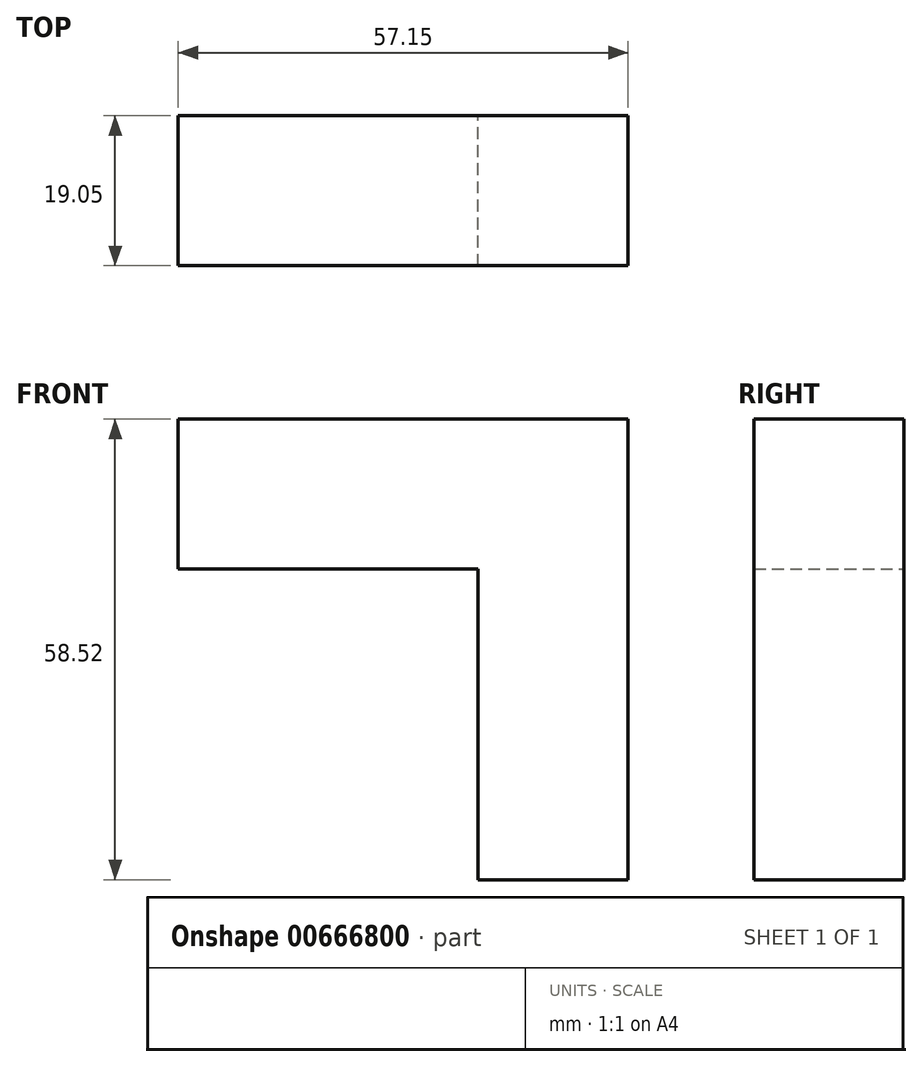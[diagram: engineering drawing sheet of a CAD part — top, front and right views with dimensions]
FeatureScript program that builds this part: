
annotation { "Feature Type Name" : "Feature", "Feature Type Description" : "" }
export const myFeature = defineFeature(function(context is Context, id is Id, definition is map)
    precondition{}
    {
        {
            var Q0;
            Q0=qCreatedBy(makeId("Front.planeOp"),FACE);
            var sketch = newSketch(context, id + "F0", { "sketchPlane" : qUnion([Q0])});
            skLineSegment(sketch, "E0", {"start": v(0, 0) * mm, "end": v(38.1, 0) * mm});
            skLineSegment(sketch, "E1", {"start": v(38.1, 0) * mm, "end": v(38.1, -39.47) * mm});
            skLineSegment(sketch, "E2", {"start": v(38.1, -39.47) * mm, "end": v(57.15, -39.47) * mm});
            skLineSegment(sketch, "E3", {"start": v(57.15, -39.47) * mm, "end": v(57.15, 19.05) * mm});
            skLineSegment(sketch, "E4", {"start": v(57.15, 19.05) * mm, "end": v(0, 19.05) * mm});
            skLineSegment(sketch, "E5", {"start": v(0, 19.05) * mm, "end": v(0, 0) * mm});
            skSolve(sketch);
        }
        {
            var Q0;
            Q0=makeQuery(id+"F0.imprint","IMPRINT",FACE,{"disambiguationData":[TD([[makeQuery(id+"F0.imprint","IMPRINT",EDGE,{"derivedFrom":sQuery(id+"F0.wireOp",EDGE,"E0")}),1.0]])]});
            extrude(context, id + "F1", {"entities" : qUnion([Q0]), "depth" : 19.05 * mm, "offsetDistance" : 25.4 * mm});
        }
    });
